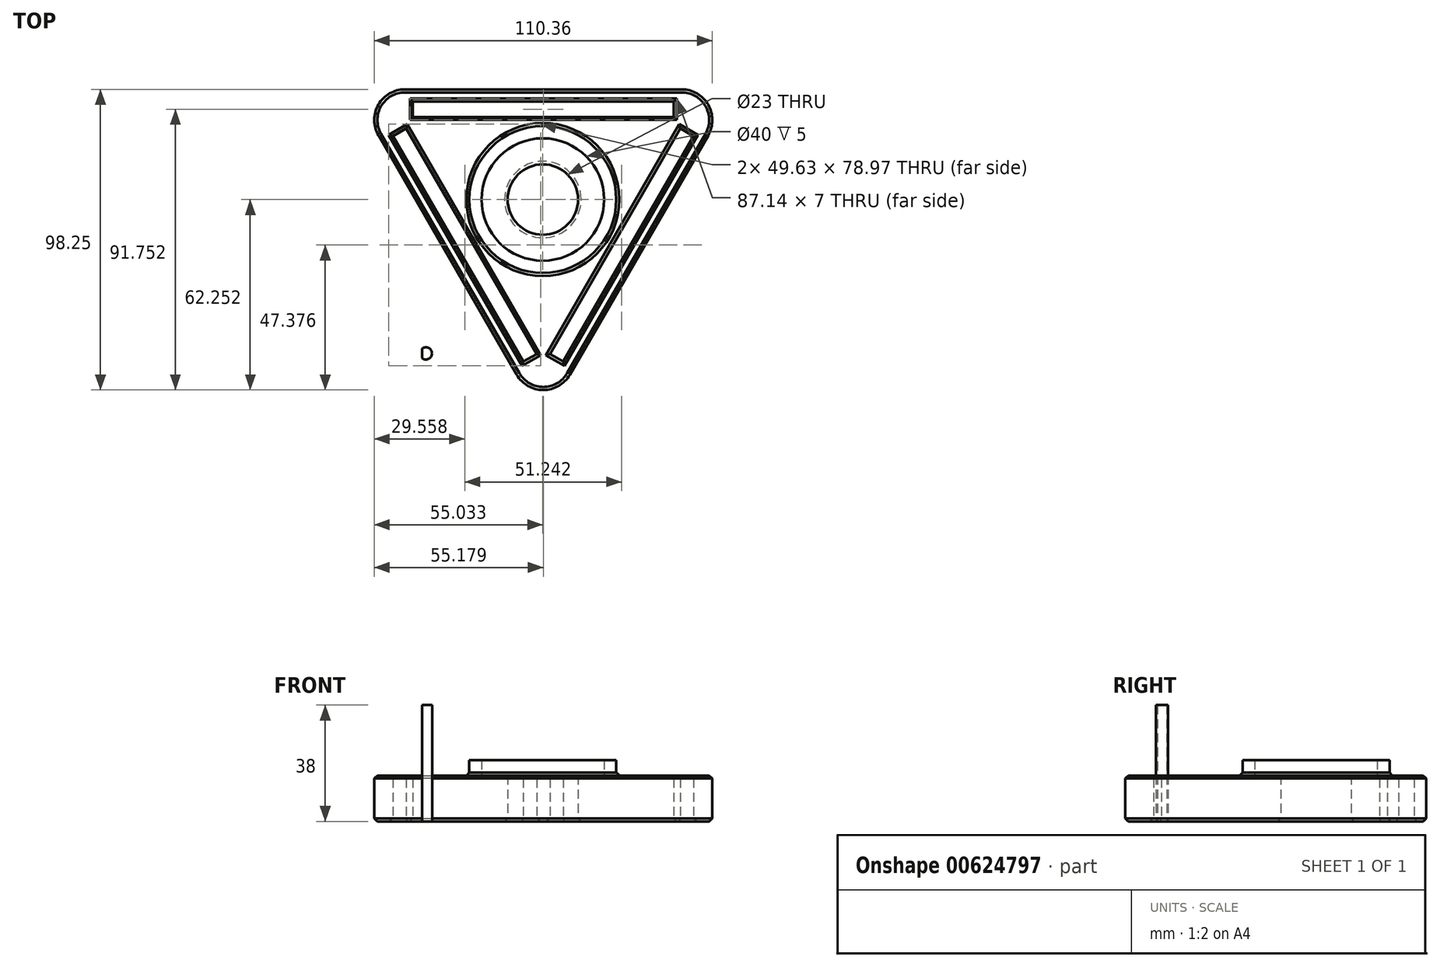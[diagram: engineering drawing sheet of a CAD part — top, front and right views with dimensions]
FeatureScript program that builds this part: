
annotation { "Feature Type Name" : "Feature", "Feature Type Description" : "" }
export const myFeature = defineFeature(function(context is Context, id is Id, definition is map)
    precondition{}
    {
        {
            var Q0;
            Q0=qCreatedBy(makeId("Top.planeOp"),FACE);
            var sketch = newSketch(context, id + "F0", { "sketchPlane" : qUnion([Q0])});
            skLineSegment(sketch, "E0", {"start": v(-18.98, 54.15) * mm, "end": v(71.38, 54.15) * mm});
            skLineSegment(sketch, "E1", {"start": v(80.04, 39.15) * mm, "end": v(34.86, -39.1) * mm});
            skLineSegment(sketch, "E2", {"start": v(-27.64, 39.15) * mm, "end": v(17.54, -39.1) * mm});
            skLineSegment(sketch, "E3", {"start": v(-22.87, 38.9) * mm, "end": v(19.7, -34.84) * mm});
            skLineSegment(sketch, "E4", {"start": v(32.7, -34.84) * mm, "end": v(75.27, 38.9) * mm});
            skLineSegment(sketch, "E5", {"start": v(68.77, 50.15) * mm, "end": v(-16.37, 50.15) * mm});
            skLineSegment(sketch, "E6.0", {"start": v(68.77, 45.15) * mm, "end": v(-16.37, 45.15) * mm});
            skLineSegment(sketch, "E6.1", {"start": v(28.37, -32.34) * mm, "end": v(70.94, 41.4) * mm});
            skLineSegment(sketch, "E6.2", {"start": v(-18.54, 41.4) * mm, "end": v(24.03, -32.34) * mm});
            skLineSegment(sketch, "E7", {"start": v(-16.37, 50.15) * mm, "end": v(-16.37, 45.15) * mm});
            skLineSegment(sketch, "E8", {"start": v(68.77, 45.15) * mm, "end": v(68.77, 50.15) * mm});
            skLineSegment(sketch, "E9", {"start": v(70.94, 41.4) * mm, "end": v(75.27, 38.9) * mm});
            skLineSegment(sketch, "E10", {"start": v(-18.54, 41.4) * mm, "end": v(-22.87, 38.9) * mm});
            skLineSegment(sketch, "E11", {"start": v(24.03, -32.34) * mm, "end": v(19.7, -34.84) * mm});
            skLineSegment(sketch, "E12", {"start": v(28.37, -32.34) * mm, "end": v(32.7, -34.84) * mm});
            skPoint(sketch, "E13.orphan", {"position": v(-29.37, 50.15) * mm});
            skPoint(sketch, "E14.orphan", {"position": v(26.2, -46.1) * mm});
            skPoint(sketch, "E15.orphan", {"position": v(81.77, 50.15) * mm});
            skPoint(sketch, "E16.visualSharp", {"position": v(-36.3, 54.15) * mm});
            skArc(sketch, "E16.filletArc", {"start": v(-18.98, 54.15) * mm, "mid": v(-27.64, 49.15) * mm, "end": v(-27.64, 39.15) * mm});
            skPoint(sketch, "E17.visualSharp", {"position": v(26.2, -54.1) * mm});
            skArc(sketch, "E17.filletArc", {"start": v(17.54, -39.1) * mm, "mid": v(26.2, -44.1) * mm, "end": v(34.86, -39.1) * mm});
            skPoint(sketch, "E18.visualSharp", {"position": v(88.7, 54.15) * mm});
            skArc(sketch, "E18.filletArc", {"start": v(80.04, 39.15) * mm, "mid": v(80.04, 49.15) * mm, "end": v(71.38, 54.15) * mm});
            skCircle(sketch, "E19", {"center": v(26.05, 18.15) * mm, "radius": 11.5 * mm});
            skSolve(sketch);
        }
        {
            var Q0;
            Q0=makeQuery(id+"F0.imprint","IMPRINT",FACE,{"disambiguationData":[TD([[makeQuery(id+"F0.imprint","IMPRINT",EDGE,{"derivedFrom":sQuery(id+"F0.wireOp",EDGE,"E0")}),-1.0]])]});
            extrude(context, id + "F1", {"entities" : qUnion([Q0]), "depth" : 15 * mm, "offsetDistance" : 25 * mm});
        }
        {
            var Q0;
            Q0=makeQuery(id+"F1.opExtrude","CAP_FACE",FACE,{"disambiguationData":[OSD([sQuery(id+"F0.wireOp",EDGE,"E0"),sQuery(id+"F0.wireOp",EDGE,"E1"),sQuery(id+"F0.wireOp",EDGE,"E2"),sQuery(id+"F0.wireOp",EDGE,"E3"),sQuery(id+"F0.wireOp",EDGE,"E4"),sQuery(id+"F0.wireOp",EDGE,"E5"),sQuery(id+"F0.wireOp",EDGE,"E6.0"),sQuery(id+"F0.wireOp",EDGE,"E6.1"),sQuery(id+"F0.wireOp",EDGE,"E6.2"),sQuery(id+"F0.wireOp",EDGE,"E7"),sQuery(id+"F0.wireOp",EDGE,"E8"),sQuery(id+"F0.wireOp",EDGE,"E9"),sQuery(id+"F0.wireOp",EDGE,"E10"),sQuery(id+"F0.wireOp",EDGE,"E11"),sQuery(id+"F0.wireOp",EDGE,"E12"),sQuery(id+"F0.wireOp",EDGE,"E16.filletArc"),sQuery(id+"F0.wireOp",EDGE,"E17.filletArc"),sQuery(id+"F0.wireOp",EDGE,"E18.filletArc"),sQuery(id+"F0.wireOp",EDGE,"E19")])],"isStart":false});
            var sketch = newSketch(context, id + "F2", { "sketchPlane" : qUnion([Q0])});
            skCircle(sketch, "E20", {"center": v(26.05, 18.15) * mm, "radius": 20 * mm});
            skCircle(sketch, "E21.0", {"center": v(26.05, 18.15) * mm, "radius": 24 * mm});
            skSolve(sketch);
        }
        {
            var Q0;
            Q0=makeQuery(id+"F2.imprint","IMPRINT",FACE,{"disambiguationData":[TD([[makeQuery(id+"F2.imprint","IMPRINT",EDGE,{"derivedFrom":sQuery(id+"F2.wireOp",EDGE,"E20")}),-1.0]])]});
            extrude(context, id + "F3", {"entities" : qUnion([Q0]), "operationType" : NewBodyOperationType.ADD, "depth" : 5 * mm, "offsetDistance" : 25 * mm});
        }
        {
            var Q0;
            {var subQ0=sQuery(id+"F0.wireOp",EDGE,"E6.2");var subQ1=sQuery(id+"F0.wireOp",EDGE,"E6.1");var subQ2=sQuery(id+"F0.wireOp",EDGE,"E6.0");var subQ3=sQuery(id+"F0.wireOp",EDGE,"E5");var subQ4=sQuery(id+"F0.wireOp",EDGE,"E4");var subQ5=sQuery(id+"F0.wireOp",EDGE,"E7");var subQ6=sQuery(id+"F0.wireOp",EDGE,"E0");var subQ7=sQuery(id+"F0.wireOp",EDGE,"E3");var subQ8=sQuery(id+"F0.wireOp",EDGE,"E1");var subQ9=sQuery(id+"F0.wireOp",EDGE,"E2");var subQ10=sQuery(id+"F0.wireOp",EDGE,"E8");var subQ11=sQuery(id+"F0.wireOp",EDGE,"E9");var subQ12=sQuery(id+"F0.wireOp",EDGE,"E10");var subQ13=sQuery(id+"F0.wireOp",EDGE,"E11");var subQ14=sQuery(id+"F0.wireOp",EDGE,"E12");var subQ15=sQuery(id+"F0.wireOp",EDGE,"E16.filletArc");var subQ16=sQuery(id+"F0.wireOp",EDGE,"E17.filletArc");var subQ17=sQuery(id+"F0.wireOp",EDGE,"E18.filletArc");Q0=makeQuery(id+"F3.boolean.opBoolean","SPLIT",FACE,{"disambiguationData":[TD([makeQuery(id+"F1.opExtrude","SWEPT_FACE",FACE,{"disambiguationData":[OSD([subQ6])]})])],"derivedFrom":makeQuery(id+"F1.opExtrude","CAP_FACE",FACE,{"disambiguationData":[OSD([subQ6,subQ8,subQ9,subQ7,subQ4,subQ3,subQ2,subQ1,subQ0,subQ5,subQ10,subQ11,subQ12,subQ13,subQ14,subQ15,subQ16,subQ17,sQuery(id+"F0.wireOp",EDGE,"E19")])],"isStart":false})});}
            chamfer(context, id + "F4", {"entities" : qUnion([Q0]), "width" : 1 * mm, "tangentPropagation" : true});
        }
        {
            var Q0;
            Q0=makeQuery(id+"F1.opExtrude","CAP_FACE",FACE,{"disambiguationData":[OSD([sQuery(id+"F0.wireOp",EDGE,"E0"),sQuery(id+"F0.wireOp",EDGE,"E1"),sQuery(id+"F0.wireOp",EDGE,"E2"),sQuery(id+"F0.wireOp",EDGE,"E3"),sQuery(id+"F0.wireOp",EDGE,"E4"),sQuery(id+"F0.wireOp",EDGE,"E5"),sQuery(id+"F0.wireOp",EDGE,"E6.0"),sQuery(id+"F0.wireOp",EDGE,"E6.1"),sQuery(id+"F0.wireOp",EDGE,"E6.2"),sQuery(id+"F0.wireOp",EDGE,"E7"),sQuery(id+"F0.wireOp",EDGE,"E8"),sQuery(id+"F0.wireOp",EDGE,"E9"),sQuery(id+"F0.wireOp",EDGE,"E10"),sQuery(id+"F0.wireOp",EDGE,"E11"),sQuery(id+"F0.wireOp",EDGE,"E12"),sQuery(id+"F0.wireOp",EDGE,"E16.filletArc"),sQuery(id+"F0.wireOp",EDGE,"E17.filletArc"),sQuery(id+"F0.wireOp",EDGE,"E18.filletArc"),sQuery(id+"F0.wireOp",EDGE,"E19")])],"isStart":true});
            chamfer(context, id + "F5", {"entities" : qUnion([Q0]), "width" : 1 * mm, "tangentPropagation" : true});
        }
        {
            var Q0;
            Q0=qCreatedBy(makeId("Top.planeOp"),FACE);
            var sketch = newSketch(context, id + "F6", { "sketchPlane" : qUnion([Q0])});
            skArc(sketch, "E22", {"start": v(-13.43, -33.66) * mm, "mid": v(-10.13, -32.14) * mm, "end": v(-13.43, -30.61) * mm});
            skLineSegment(sketch, "E23", {"start": v(-13.43, -33.66) * mm, "end": v(-13.43, -30.61) * mm});
            skSolve(sketch);
        }
        {
            var Q0;
            Q0=makeQuery(id+"F6.imprint","IMPRINT",FACE,{"disambiguationData":[TD([[makeQuery(id+"F6.imprint","IMPRINT",EDGE,{"derivedFrom":sQuery(id+"F6.wireOp",EDGE,"E22")}),1.0]])]});
            extrude(context, id + "F7", {"entities" : qUnion([Q0]), "depth" : 38 * mm, "offsetDistance" : 25 * mm});
        }
    });
